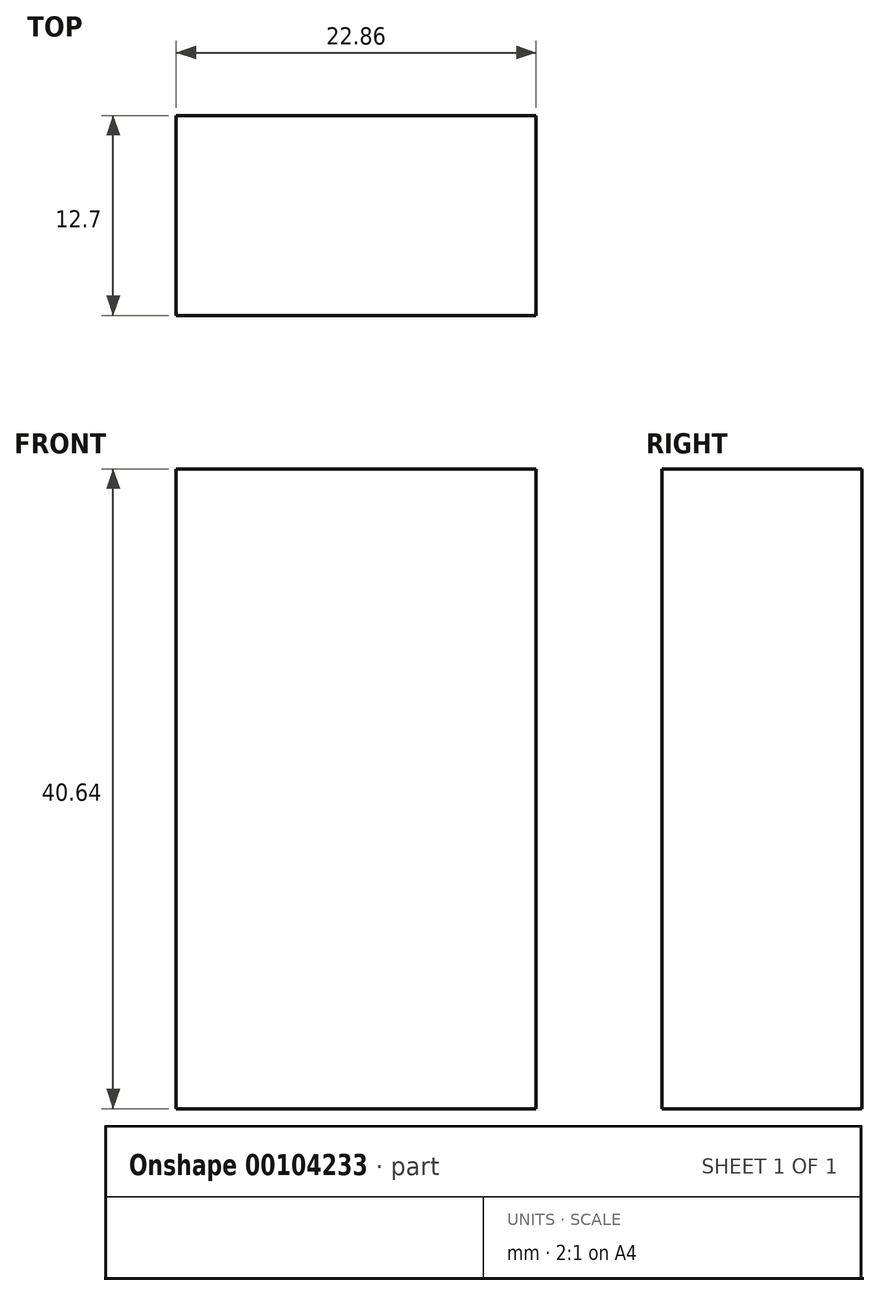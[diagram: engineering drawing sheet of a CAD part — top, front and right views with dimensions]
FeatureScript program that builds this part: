
annotation { "Feature Type Name" : "Feature", "Feature Type Description" : "" }
export const myFeature = defineFeature(function(context is Context, id is Id, definition is map)
    precondition{}
    {
        {
            var Q0;
            Q0=qCreatedBy(makeId("Front.planeOp"),FACE);
            var sketch = newSketch(context, id + "F0", { "sketchPlane" : qUnion([Q0])});
            skLineSegment(sketch, "E0.bottom", {"start": v(-43.3, 21.8) * mm, "end": v(-20.44, 21.8) * mm});
            skLineSegment(sketch, "E0.top", {"start": v(-43.3, -18.83) * mm, "end": v(-20.44, -18.83) * mm});
            skLineSegment(sketch, "E0.left", {"start": v(-43.3, 21.8) * mm, "end": v(-43.3, -18.83) * mm});
            skLineSegment(sketch, "E0.right", {"start": v(-20.44, 21.8) * mm, "end": v(-20.44, -18.83) * mm});
            skSolve(sketch);
        }
        {
            var Q0;
            Q0=makeQuery(id+"F0.imprint","IMPRINT",FACE,{"disambiguationData":[TD([[makeQuery(id+"F0.imprint","IMPRINT",EDGE,{"derivedFrom":sQuery(id+"F0.wireOp",EDGE,"E0.bottom")}),-1.0]])]});
            extrude(context, id + "F1", {"entities" : qUnion([Q0]), "depth" : 12.7 * mm});
        }
    });
